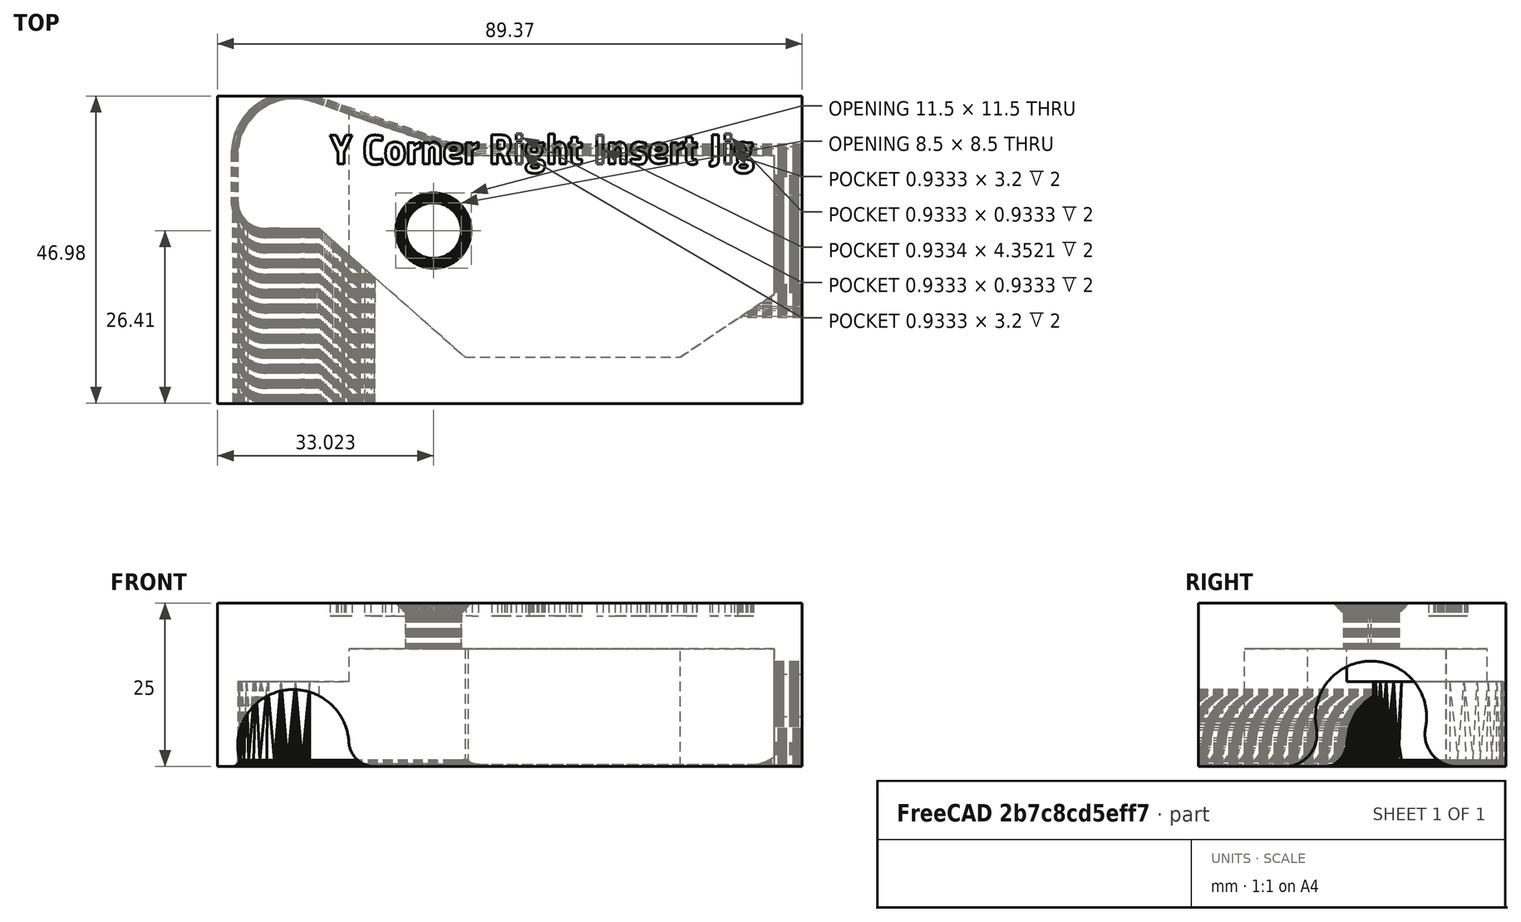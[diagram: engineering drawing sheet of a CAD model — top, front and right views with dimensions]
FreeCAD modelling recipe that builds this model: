
FCSTD DOCUMENT  (FreeCAD 0.17R9537 (Git))
Label: y_corner_right_insert_jig1.1
License: All rights reserved
LicenseURL: http://en.wikipedia.org/wiki/All_rights_reserved
objects: Part::Feature×3, Mesh::Feature×1, Part::Part2DObjectPython×1, PartDesign::Pocket×1, PartDesign::Body×1
note: 7 computed .brp shape members not serialized (recipe doc carries the construction recipe); baked Part::Feature solids carry a one-line shape summary decoded from their .brp

FEATURE [Mesh::Feature] yright
FEATURE [Part::Feature] yright001
  shape: bbox 89.37 x 46.99 x 25 mm, 5510 faces, 0 solids (baked)
FEATURE [Part::Feature] yright001_solid  label="yright001 (Solid)"
  shape: bbox 89.37 x 46.99 x 25 mm, 5510 faces (baked)
FEATURE [Part::Feature] yright001_solid001  label="yright001 (Solid)001"
  shape: bbox 89.37 x 46.99 x 25 mm, 4035 faces (baked)
FEATURE [Part::Part2DObjectPython] ShapeString  # Draft 2D object (typed FeaturePython)
  FontFile = <userpath>/Desktop/Titillium-BoldUpright.otf
  Placement = pos=(-24,19,25) rot=(0,0,1;0rad)
  Size = 2.5
  String = Y Corner Right Insert Jig
  Support = -> [yright001_solid001]
  Tracking = 70
FEATURE [PartDesign::Pocket] Pocket
  Length = 2
  Profile = -> ShapeString
  Type = 0
FEATURE [PartDesign::Body] Body
  Model = -> [Pocket]
  Origin = -> BodyOrigin
  Tip = -> Pocket
